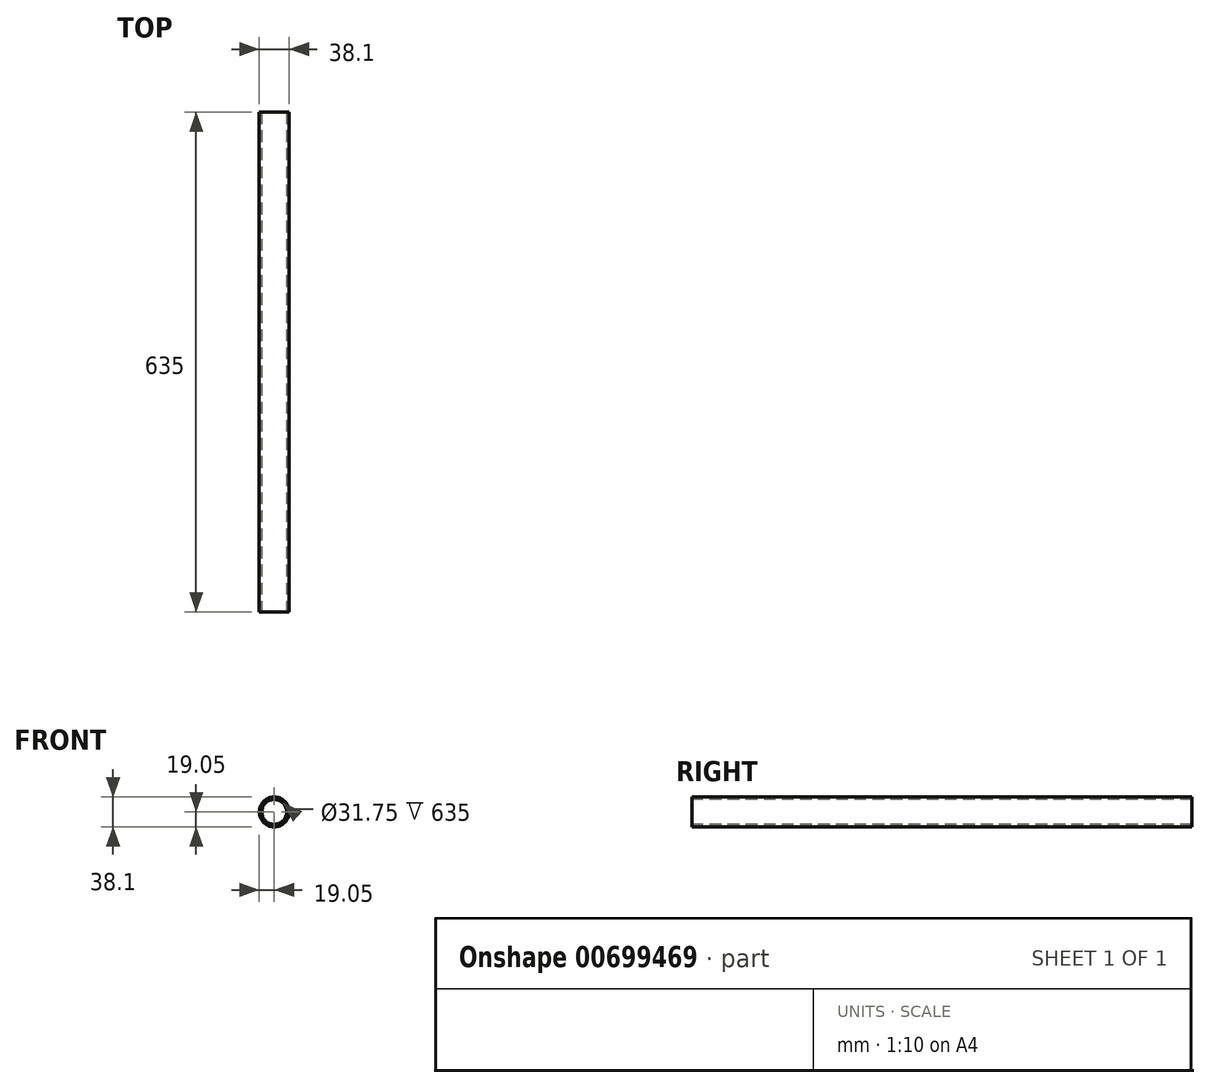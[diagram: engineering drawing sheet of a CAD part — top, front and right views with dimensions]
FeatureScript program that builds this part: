
annotation { "Feature Type Name" : "Feature", "Feature Type Description" : "" }
export const myFeature = defineFeature(function(context is Context, id is Id, definition is map)
    precondition{}
    {
        {
            var Q0;
            Q0=qCreatedBy(makeId("Front.planeOp"),FACE);
            var sketch = newSketch(context, id + "F0", { "sketchPlane" : qUnion([Q0])});
            skCircle(sketch, "E0", {"center": v(0, 0) * mm, "radius": 19.05 * mm});
            skCircle(sketch, "E1", {"center": v(0, 0) * mm, "radius": 15.88 * mm});
            skSolve(sketch);
        }
        {
            var Q0;
            Q0 = qSketchRegion(id + "F0", true);
            extrude(context, id + "F1", {"entities" : qUnion([Q0]), "oppositeDirection" : true, "depth" : 635 * mm, "offsetDistance" : 25.4 * mm});
        }
    });
